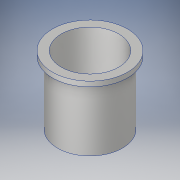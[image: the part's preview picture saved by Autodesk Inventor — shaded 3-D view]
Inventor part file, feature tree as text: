
AUTODESK INVENTOR PART (.ipt)
format: ipt  version: 2017 SP1 (Build 210196100, 196)  size: 159,232 bytes
history: native  units: in
note: dims shown in document units (in); Inventor stores cm internally (conversion verified against a paired STEP export)
features: revolve x1, sketch x1
ambient origin geometry x8: Origin, YZ Plane, XZ Plane, XY Plane, X Axis, Y Axis, Z Axis, Center Point
bodies: Solid1 (feature_tree)
feature tree (2):
  revolve  "Revolution1"  [1 undecoded]
  sketch  "Sketch1"  dims[d0=1.13in d1=3.75in d2=0.125in d3=0.1718in d5=1.0in d6=1.0in d7=90.0deg d8=0.5in d9=15.0deg d12=1.25in d13=0.25in d16=0.5in d17=0.5in d18=0.5in d19=2.5in d20=0.5in d22=0.375in d23=0.25in d25=0.234in d27=0.125in d28=0.25in d29=1.0in d30=4.25in d31=0.25in d33=0.8014in d34=15.0deg d35=0.125in d36=1.0in d37=90.0deg]
note: 1 required parameter value undecoded (feature->parameter linkage not recoverable at this tier; creation-order binding heuristic only, values carry confidence <= 0.55)
